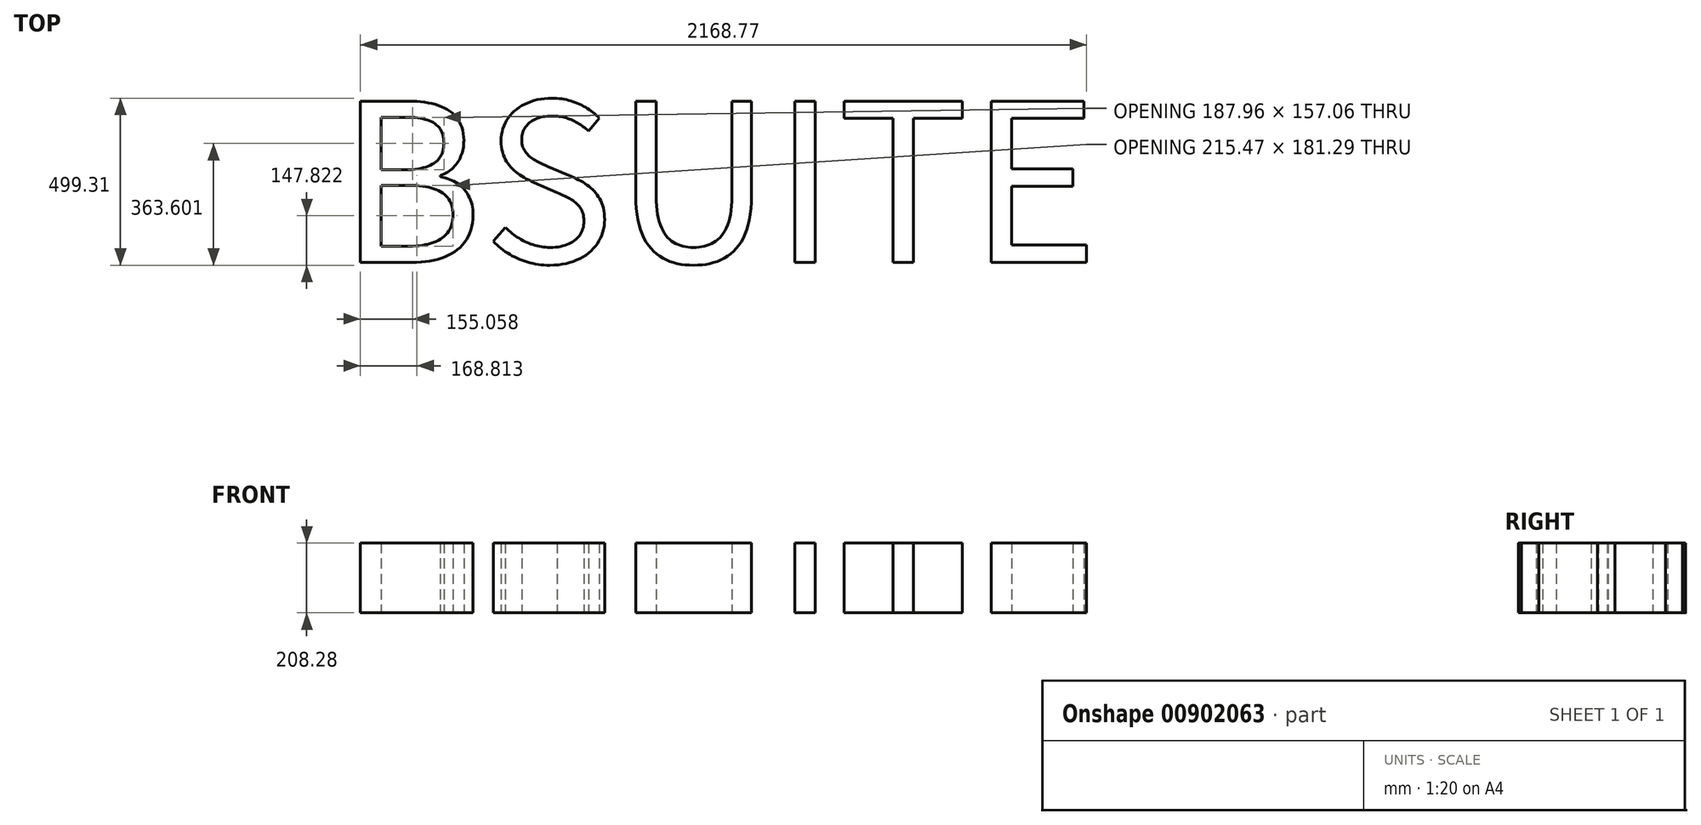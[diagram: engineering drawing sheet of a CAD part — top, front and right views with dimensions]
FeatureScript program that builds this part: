
annotation { "Feature Type Name" : "Feature", "Feature Type Description" : "" }
export const myFeature = defineFeature(function(context is Context, id is Id, definition is map)
    precondition{}
    {
        {
            var Q0;
            Q0=qCreatedBy(makeId("Top.planeOp"),FACE);
            var sketch = newSketch(context, id + "F0", { "sketchPlane" : qUnion([Q0])});
            skText(sketch, "E0", { "text": "BSUITE", "fontName": "NotoSansCJKkr-Regular.otf"});
            const initialGuessF0  = {"E0": [-1.40552, 0.05122, 1, 0, 0.47303]};
            skSetInitialGuess(sketch, initialGuessF0);
            skSolve(sketch);
        }
        {
            var Q0;
            Q0 = qSketchRegion(id + "F0", true);
            extrude(context, id + "F1", {"entities" : qUnion([Q0]), "depth" : 208.28 * mm, "offsetDistance" : 25.4 * mm});
        }
    });
